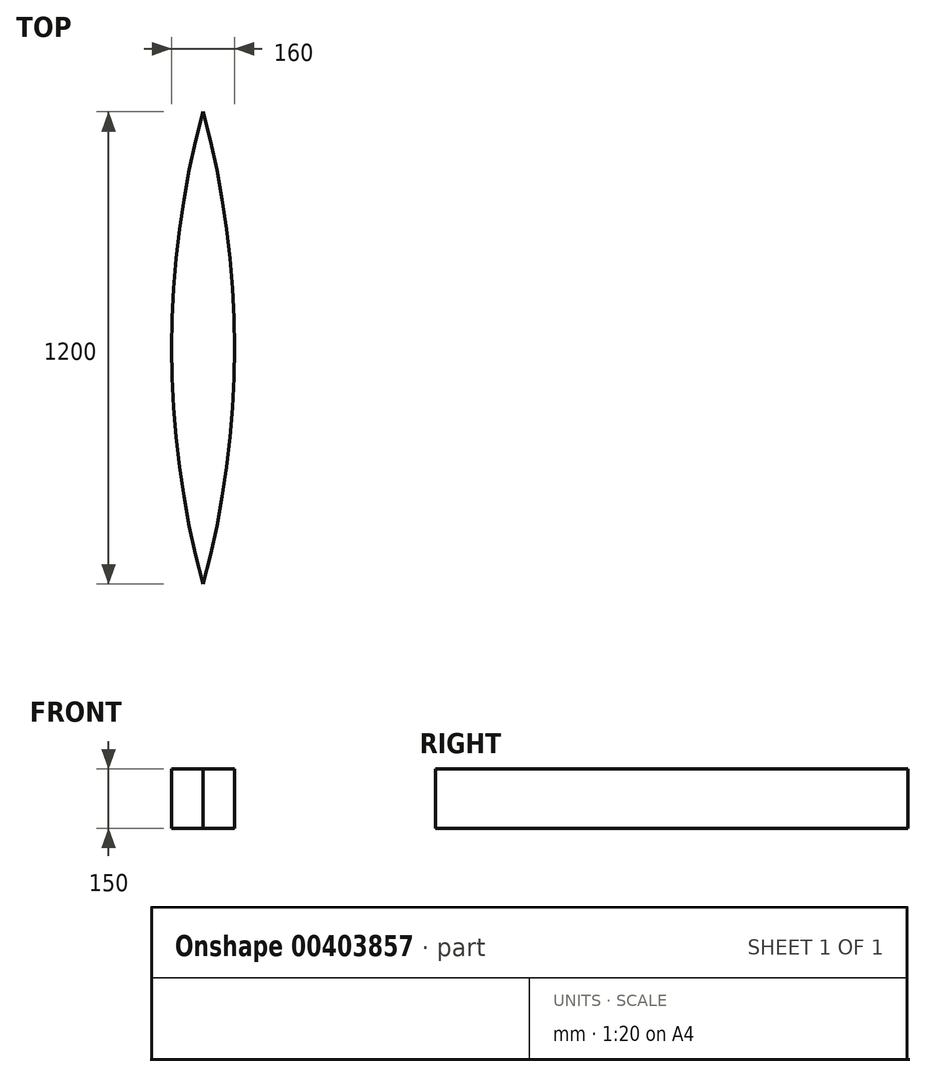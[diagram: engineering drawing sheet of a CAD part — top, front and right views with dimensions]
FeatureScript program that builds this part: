
annotation { "Feature Type Name" : "Feature", "Feature Type Description" : "" }
export const myFeature = defineFeature(function(context is Context, id is Id, definition is map)
    precondition{}
    {
        {
            var Q0;
            Q0=qCreatedBy(makeId("Top.planeOp"),FACE);
            var sketch = newSketch(context, id + "F0", { "sketchPlane" : qUnion([Q0])});
            skLineSegment(sketch, "E0", {"start": v(0, 600) * mm, "end": v(0, 0) * mm});
            skLineSegment(sketch, "E1", {"start": v(0, 0) * mm, "end": v(80, 0) * mm});
            skArc(sketch, "E2", {"start": v(80, 0) * mm, "mid": v(59.91, 302.65) * mm, "end": v(0, 600) * mm});
            skLineSegment(sketch, "E3", {"start": v(80, 0) * mm, "end": v(80, -248.99) * mm, "construction": true});
            skSolve(sketch);
        }
        {
            var Q0;
            Q0 = qSketchRegion(id + "F0", true);
            var Q1;
            Q1 = qBodyType(qCreatedBy(id + "F0" ,EDGE), BodyType.WIRE);
            extrude(context, id + "F1", {"entities" : qUnion([Q0]), "surfaceEntities" : qUnion([Q1]), "depth" : 150 * mm});
        }
        {
            var Q0;
            Q0=makeQuery(id+"F1.opExtrude","SWEPT_BODY",BODY,{"disambiguationData":[OSD([sQuery(id+"F0.wireOp",EDGE,"E0"),sQuery(id+"F0.wireOp",EDGE,"E1"),sQuery(id+"F0.wireOp",EDGE,"E2")])]});
            var Q1;
            Q1=makeQuery(id+"F1.opExtrude","SWEPT_FACE",FACE,{"disambiguationData":[OSD([sQuery(id+"F0.wireOp",EDGE,"E0")])]});
            mirror(context, id + "F2", {"operationType" : NewBodyOperationType.ADD, "entities" : qUnion([Q0]), "mirrorPlane" : qUnion([Q1])});
        }
        {
            var Q0;
            Q0=makeQuery(id+"F1.opExtrude","SWEPT_BODY",BODY,{"disambiguationData":[OSD([sQuery(id+"F0.wireOp",EDGE,"E0"),sQuery(id+"F0.wireOp",EDGE,"E1"),sQuery(id+"F0.wireOp",EDGE,"E2")])]});
            var Q1;
            Q1=qCreatedBy(makeId("Front.planeOp"),FACE);
            mirror(context, id + "F3", {"operationType" : NewBodyOperationType.ADD, "entities" : qUnion([Q0]), "mirrorPlane" : qUnion([Q1])});
        }
    });
